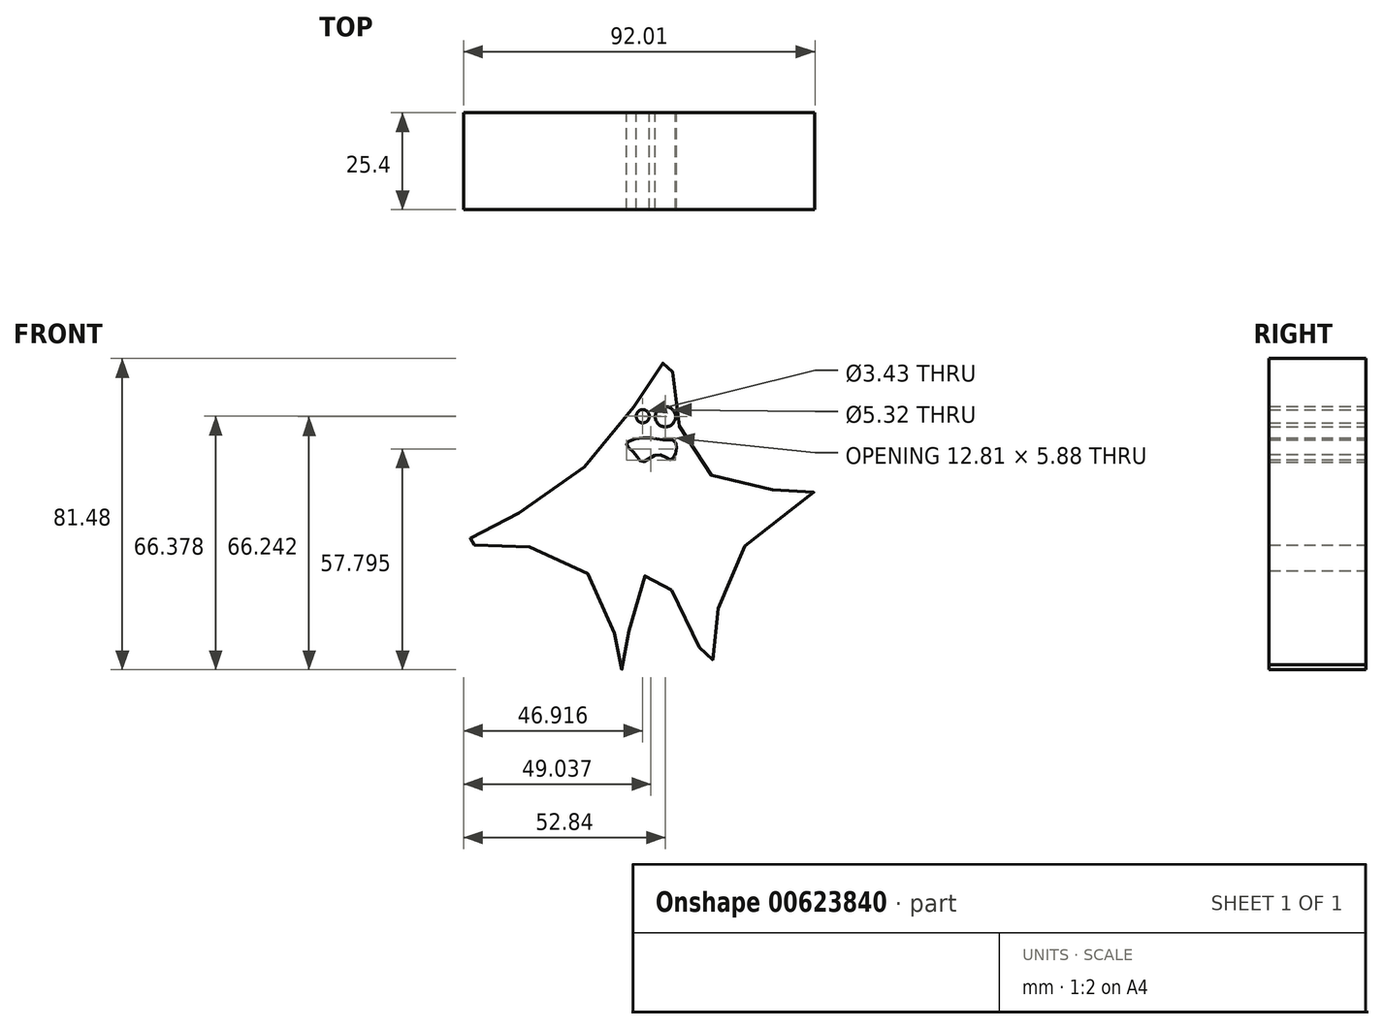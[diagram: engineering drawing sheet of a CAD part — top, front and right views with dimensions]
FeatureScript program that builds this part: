
annotation { "Feature Type Name" : "Feature", "Feature Type Description" : "" }
export const myFeature = defineFeature(function(context is Context, id is Id, definition is map)
    precondition{}
    {
        {
            var Q0;
            Q0=qCreatedBy(makeId("Front.planeOp"),FACE);
            var sketch = newSketch(context, id + "F0", { "sketchPlane" : qUnion([Q0])});
            skPoint(sketch, "E0", {"position": v(0, 0) * mm});
            skFitSpline(sketch, "E1", {"points": [v(0, 0) * mm, v(22.43, 28.26) * mm, v(30.37, 0) * mm, v(60.33, -6.72) * mm, v(38.95, -25.02) * mm, v(32.64, -51.59) * mm, v(17.57, -27.13) * mm, v(9.96, -52.88) * mm, v(0, -26.97) * mm, v(-31.5, -20.16) * mm, v(0, 0) * mm]});
            skPoint(sketch, "E2", {"position": v(13.94, 12.18) * mm});
            skPoint(sketch, "E3", {"position": v(20.69, 12.18) * mm});
            skSolve(sketch);
        }
        {
            var Q0;
            Q0=makeQuery(id+"F0.imprint","IMPRINT",FACE,{"disambiguationData":[TD([[makeQuery(id+"F0.imprint","IMPRINT",EDGE,{"derivedFrom":sQuery(id+"F0.wireOp",EDGE,"E1")}),-1.0]])]});
            extrude(context, id + "F1", {"entities" : qUnion([Q0]), "depth" : 25.4 * mm, "offsetDistance" : 25.4 * mm});
        }
        {
            var Q0;
            Q0=qCreatedBy(makeId("Front.planeOp"),FACE);
            var sketch = newSketch(context, id + "F2", { "sketchPlane" : qUnion([Q0])});
            skCircle(sketch, "E4", {"center": v(15.3, 13.34) * mm, "radius": 1.71 * mm});
            skCircle(sketch, "E5", {"center": v(21.23, 13.2) * mm, "radius": 2.66 * mm});
            skFitSpline(sketch, "E6", {"points": [v(15.39, 7.7) * mm, v(11.01, 6.07) * mm, v(13.36, 3.4) * mm, v(15.3, 1.38) * mm, v(19.44, 3.32) * mm, v(22.6, 1.94) * mm, v(23.89, 3.73) * mm, v(23.65, 6.8) * mm, v(20.73, 7.2) * mm, v(15.39, 7.7) * mm]});
            skSolve(sketch);
        }
        {
            var Q0;
            Q0 = qSketchRegion(id + "F2", true);
            extrude(context, id + "F3", {"entities" : qUnion([Q0]), "operationType" : NewBodyOperationType.REMOVE, "oppositeDirection" : true, "depth" : 25.4 * mm, "offsetDistance" : 25.4 * mm});
        }
        {
            var Q0;
            Q0 = qSketchRegion(id + "F2", true);
            extrude(context, id + "F4", {"entities" : qUnion([Q0]), "operationType" : NewBodyOperationType.REMOVE, "endBound" : BoundingType.SYMMETRIC, "depth" : 115.32 * mm, "offsetDistance" : 25.4 * mm});
        }
    });
